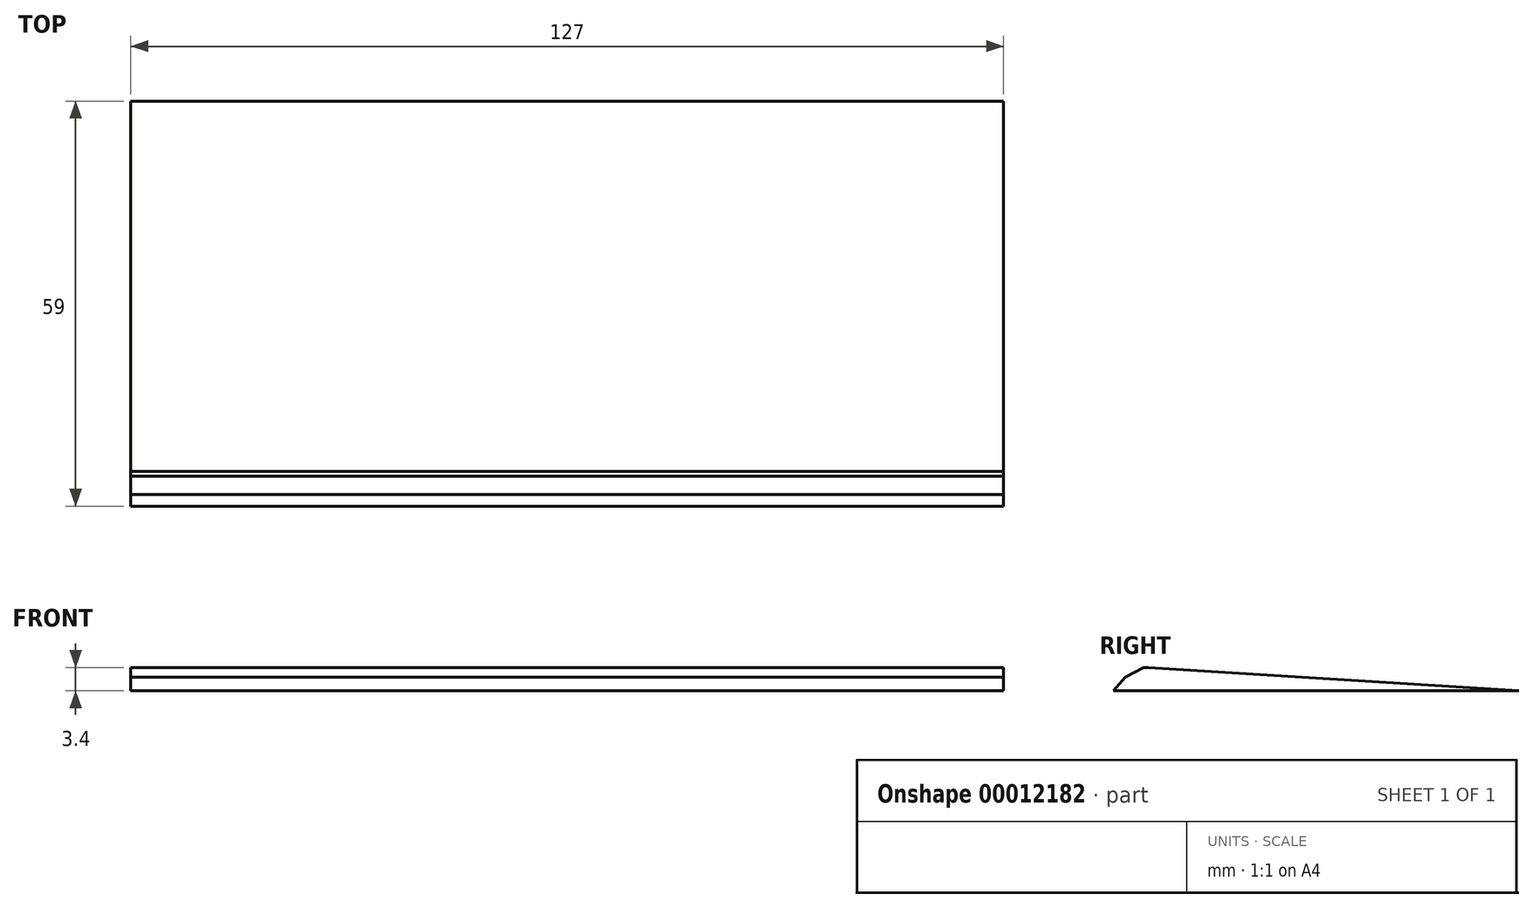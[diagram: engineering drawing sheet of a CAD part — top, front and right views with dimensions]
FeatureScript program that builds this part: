
annotation { "Feature Type Name" : "Feature", "Feature Type Description" : "" }
export const myFeature = defineFeature(function(context is Context, id is Id, definition is map)
    precondition{}
    {
        {
            var Q0;
            Q0=qCreatedBy(makeId("Right.planeOp"),FACE);
            var sketch = newSketch(context, id + "F0", { "sketchPlane" : qUnion([Q0])});
            skLineSegment(sketch, "E0", {"start": v(-37.2, 12.76) * mm, "end": v(21.79, 12.76) * mm});
            skLineSegment(sketch, "E1", {"start": v(21.79, 12.76) * mm, "end": v(-32.16, 16.16) * mm});
            skLineSegment(sketch, "E2", {"start": v(-29.77, 16.16) * mm, "end": v(-32.16, 16.16) * mm});
            skLineSegment(sketch, "E3", {"start": v(-29.77, 16.16) * mm, "end": v(-30.55, 16.16) * mm});
            skLineSegment(sketch, "E4", {"start": v(-30.55, 16.16) * mm, "end": v(-32.83, 16.16) * mm});
            skLineSegment(sketch, "E5", {"start": v(-32.83, 16.16) * mm, "end": v(-35.52, 14.72) * mm});
            skLineSegment(sketch, "E6", {"start": v(-35.52, 14.72) * mm, "end": v(-37.2, 12.76) * mm});
            skSolve(sketch);
        }
        {
            var Q0;
            Q0=makeQuery(id+"F0.imprint","IMPRINT",FACE,{"disambiguationData":[TD([[makeQuery(id+"F0.imprint","IMPRINT",EDGE,{"derivedFrom":sQuery(id+"F0.wireOp",EDGE,"E0")}),1.0]])]});
            extrude(context, id + "F1", {"entities" : qUnion([Q0]), "depth" : 127 * mm});
        }
    });
